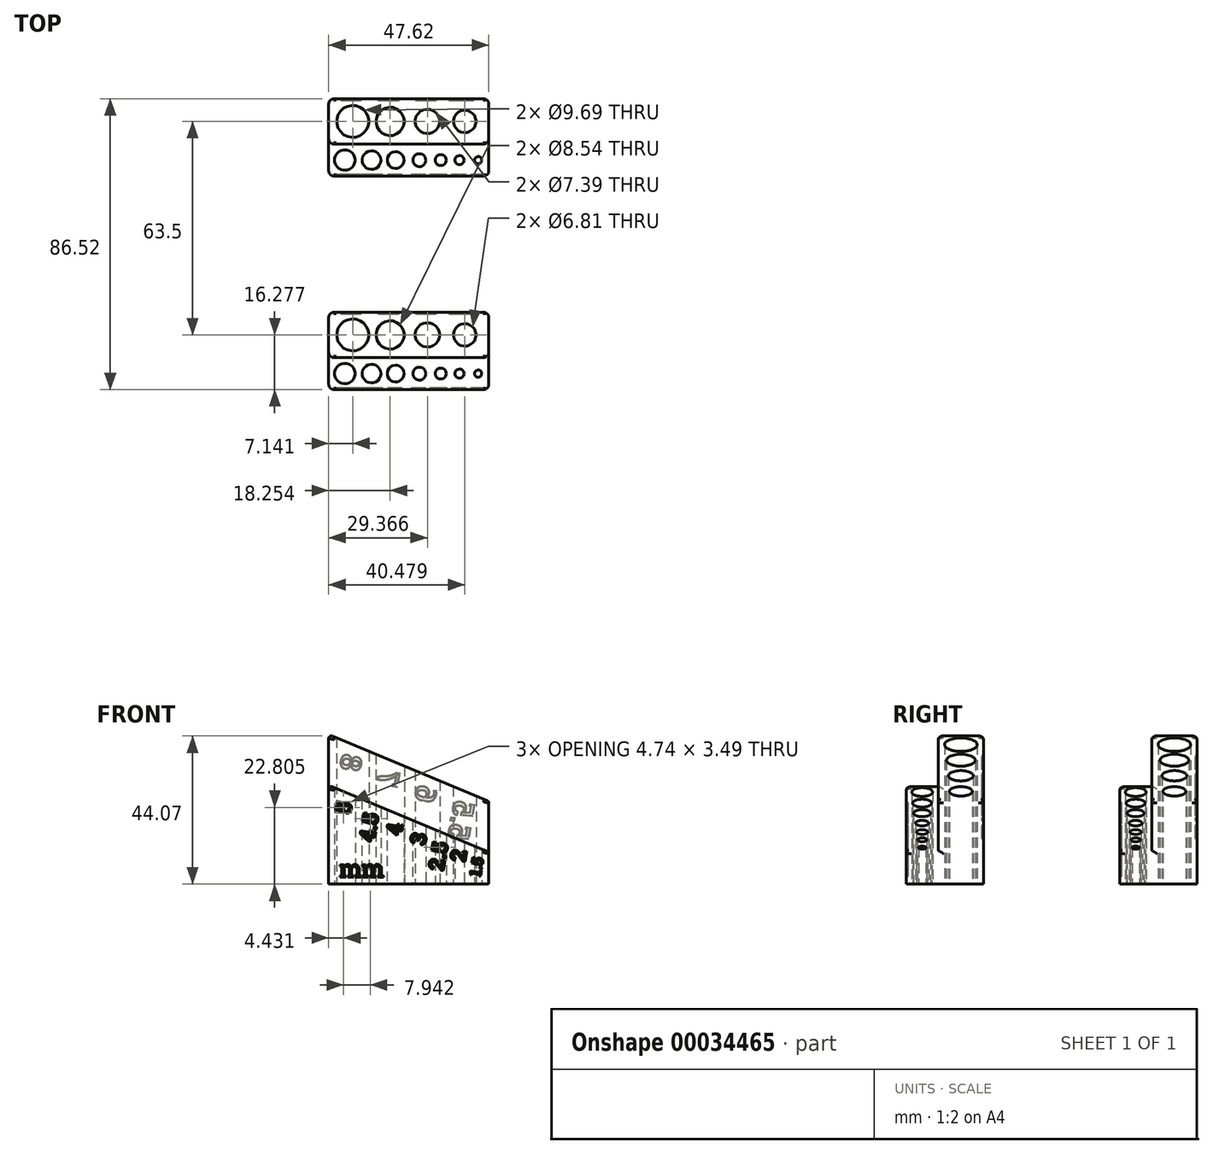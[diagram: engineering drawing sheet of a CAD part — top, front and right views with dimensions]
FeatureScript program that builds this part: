
annotation { "Feature Type Name" : "Feature", "Feature Type Description" : "" }
export const myFeature = defineFeature(function(context is Context, id is Id, definition is map)
    precondition{}
    {
        {
            var Q0;
            Q0=qCreatedBy(makeId("Front.planeOp"),FACE);
            var sketch = newSketch(context, id + "F0", { "sketchPlane" : qUnion([Q0])});
            skLineSegment(sketch, "E0", {"start": v(-23.81, 0) * mm, "end": v(23.81, 0) * mm});
            skLineSegment(sketch, "E1", {"start": v(23.81, 0) * mm, "end": v(23.81, 9.53) * mm});
            skLineSegment(sketch, "E2", {"start": v(23.81, 9.53) * mm, "end": v(-23.81, 29.37) * mm});
            skLineSegment(sketch, "E3", {"start": v(-23.81, 29.37) * mm, "end": v(-23.81, 0) * mm});
            skLineSegment(sketch, "E4", {"start": v(0, 0) * mm, "end": v(0, 19.45) * mm, "construction": true});
            skSolve(sketch);
        }
        {
            var Q0;
            Q0=qSketchRegion(id+"F0",true);
            extrude(context, id + "F1", {"entities" : qUnion([Q0]), "depth" : 9.52 * mm});
        }
        {
            var Q0;
            Q0=qCreatedBy(makeId("Front.planeOp"),FACE);
            var sketch = newSketch(context, id + "F2", { "sketchPlane" : qUnion([Q0])});
            skLineSegment(sketch, "E5.0", {"start": v(-23.81, 0) * mm, "end": v(23.81, 0) * mm});
            skLineSegment(sketch, "E6", {"start": v(23.81, 0) * mm, "end": v(23.81, 24.6) * mm});
            skLineSegment(sketch, "E7", {"start": v(-23.81, 0) * mm, "end": v(-23.81, 44.45) * mm});
            skLineSegment(sketch, "E8", {"start": v(-23.81, 44.45) * mm, "end": v(23.81, 24.6) * mm});
            skLineSegment(sketch, "E9.0", {"start": v(23.81, 9.52) * mm, "end": v(-23.81, 29.37) * mm, "construction": true});
            skSolve(sketch);
        }
        {
            var Q0;
            Q0=qSketchRegion(id+"F2",true);
            extrude(context, id + "F3", {"entities" : qUnion([Q0]), "operationType" : NewBodyOperationType.ADD, "oppositeDirection" : true, "depth" : 13.5 * mm});
        }
        {
            var Q0;
            Q0=qCreatedBy(makeId("Top.planeOp"),FACE);
            var sketch = newSketch(context, id + "F4", { "sketchPlane" : qUnion([Q0])});
            skLineSegment(sketch, "E10.0", {"start": v(23.81, 0) * mm, "end": v(-23.81, 0) * mm, "construction": true});
            skLineSegment(sketch, "E11.bottom", {"start": v(23.81, -9.53) * mm, "end": v(-23.81, -9.53) * mm, "construction": true});
            skLineSegment(sketch, "E11.top", {"start": v(23.81, 13.5) * mm, "end": v(-23.81, 13.5) * mm, "construction": true});
            skLineSegment(sketch, "E12", {"start": v(23.81, -4.76) * mm, "end": v(-23.81, -4.76) * mm, "construction": true});
            skLineSegment(sketch, "E13", {"start": v(23.81, -9.53) * mm, "end": v(23.81, 0) * mm, "construction": true});
            skLineSegment(sketch, "E14", {"start": v(-23.81, -9.53) * mm, "end": v(-23.81, 0) * mm, "construction": true});
            skLineSegment(sketch, "E15", {"start": v(-23.81, 13.5) * mm, "end": v(-23.81, 0) * mm, "construction": true});
            skLineSegment(sketch, "E16", {"start": v(23.81, 0) * mm, "end": v(23.81, 13.5) * mm, "construction": true});
            skCircle(sketch, "E17", {"center": v(20.64, -4.76) * mm, "radius": 0.87 * mm, "construction": true});
            skLineSegment(sketch, "E18", {"start": v(21.39, -5.2) * mm, "end": v(21.39, -4.33) * mm, "construction": true});
            skLineSegment(sketch, "E19", {"start": v(21.39, -4.33) * mm, "end": v(20.64, -3.9) * mm, "construction": true});
            skLineSegment(sketch, "E20", {"start": v(19.89, -5.2) * mm, "end": v(20.64, -5.63) * mm, "construction": true});
            skLineSegment(sketch, "E21", {"start": v(20.64, -5.63) * mm, "end": v(21.39, -5.2) * mm, "construction": true});
            skLineSegment(sketch, "E22", {"start": v(19.89, -5.2) * mm, "end": v(19.89, -4.33) * mm, "construction": true});
            skLineSegment(sketch, "E23", {"start": v(19.89, -4.33) * mm, "end": v(20.64, -3.9) * mm, "construction": true});
            skCircle(sketch, "E24", {"center": v(20.64, -4.76) * mm, "radius": 1.1 * mm});
            skLineSegment(sketch, "E25", {"start": v(20.64, -5.63) * mm, "end": v(20.64, -5.86) * mm, "construction": true});
            skCircle(sketch, "E26", {"center": v(15.08, -4.76) * mm, "radius": 1.15 * mm, "construction": true});
            skLineSegment(sketch, "E27", {"start": v(16.08, -5.34) * mm, "end": v(16.08, -4.19) * mm, "construction": true});
            skLineSegment(sketch, "E28", {"start": v(16.08, -4.19) * mm, "end": v(15.08, -3.6) * mm, "construction": true});
            skLineSegment(sketch, "E29", {"start": v(14.08, -5.34) * mm, "end": v(15.08, -5.92) * mm, "construction": true});
            skLineSegment(sketch, "E30", {"start": v(15.08, -5.92) * mm, "end": v(16.08, -5.34) * mm, "construction": true});
            skLineSegment(sketch, "E31", {"start": v(14.08, -5.34) * mm, "end": v(14.08, -4.19) * mm, "construction": true});
            skLineSegment(sketch, "E32", {"start": v(14.08, -4.19) * mm, "end": v(15.08, -3.6) * mm, "construction": true});
            skCircle(sketch, "E33", {"center": v(15.08, -4.76) * mm, "radius": 1.38 * mm});
            skLineSegment(sketch, "E34", {"start": v(15.08, -5.92) * mm, "end": v(15.08, -6.15) * mm, "construction": true});
            skCircle(sketch, "E35", {"center": v(9.52, -4.76) * mm, "radius": 1.44 * mm, "construction": true});
            skLineSegment(sketch, "E36", {"start": v(10.77, -5.48) * mm, "end": v(10.77, -4.04) * mm, "construction": true});
            skLineSegment(sketch, "E37", {"start": v(10.78, -4.04) * mm, "end": v(9.53, -3.32) * mm, "construction": true});
            skLineSegment(sketch, "E38", {"start": v(8.28, -5.48) * mm, "end": v(9.53, -6.2) * mm, "construction": true});
            skLineSegment(sketch, "E39", {"start": v(9.53, -6.2) * mm, "end": v(10.77, -5.48) * mm, "construction": true});
            skLineSegment(sketch, "E40", {"start": v(8.27, -5.48) * mm, "end": v(8.27, -4.04) * mm, "construction": true});
            skLineSegment(sketch, "E41", {"start": v(8.27, -4.04) * mm, "end": v(9.53, -3.32) * mm, "construction": true});
            skCircle(sketch, "E42", {"center": v(9.52, -4.76) * mm, "radius": 1.67 * mm});
            skLineSegment(sketch, "E43", {"start": v(9.53, -6.2) * mm, "end": v(9.53, -6.43) * mm, "construction": true});
            skCircle(sketch, "E44", {"center": v(3.17, -4.76) * mm, "radius": 1.73 * mm, "construction": true});
            skLineSegment(sketch, "E45", {"start": v(4.68, -5.63) * mm, "end": v(4.68, -3.9) * mm, "construction": true});
            skLineSegment(sketch, "E46", {"start": v(4.67, -3.9) * mm, "end": v(3.18, -3.03) * mm, "construction": true});
            skLineSegment(sketch, "E47", {"start": v(1.68, -5.63) * mm, "end": v(3.18, -6.5) * mm, "construction": true});
            skLineSegment(sketch, "E48", {"start": v(3.18, -6.5) * mm, "end": v(4.68, -5.63) * mm, "construction": true});
            skLineSegment(sketch, "E49", {"start": v(1.68, -5.63) * mm, "end": v(1.68, -3.9) * mm, "construction": true});
            skLineSegment(sketch, "E50", {"start": v(1.68, -3.9) * mm, "end": v(3.18, -3.03) * mm, "construction": true});
            skCircle(sketch, "E51", {"center": v(3.17, -4.76) * mm, "radius": 1.96 * mm});
            skLineSegment(sketch, "E52", {"start": v(3.18, -6.5) * mm, "end": v(3.18, -6.72) * mm, "construction": true});
            skCircle(sketch, "E53", {"center": v(-3.94, -4.76) * mm, "radius": 2.3 * mm, "construction": true});
            skLineSegment(sketch, "E54", {"start": v(-1.94, -5.92) * mm, "end": v(-1.94, -3.6) * mm, "construction": true});
            skLineSegment(sketch, "E55", {"start": v(-1.94, -3.6) * mm, "end": v(-3.94, -2.45) * mm, "construction": true});
            skLineSegment(sketch, "E56", {"start": v(-5.94, -5.92) * mm, "end": v(-3.94, -7.07) * mm, "construction": true});
            skLineSegment(sketch, "E57", {"start": v(-3.94, -7.07) * mm, "end": v(-1.94, -5.92) * mm, "construction": true});
            skLineSegment(sketch, "E58", {"start": v(-5.94, -5.92) * mm, "end": v(-5.94, -3.6) * mm, "construction": true});
            skLineSegment(sketch, "E59", {"start": v(-5.94, -3.6) * mm, "end": v(-3.94, -2.45) * mm, "construction": true});
            skCircle(sketch, "E60", {"center": v(-3.94, -4.76) * mm, "radius": 2.54 * mm});
            skLineSegment(sketch, "E61", {"start": v(-3.94, -7.07) * mm, "end": v(-3.94, -7.3) * mm, "construction": true});
            skCircle(sketch, "E62", {"center": v(-11.08, -4.76) * mm, "radius": 2.6 * mm, "construction": true});
            skLineSegment(sketch, "E63", {"start": v(-8.83, -6.06) * mm, "end": v(-8.83, -3.46) * mm, "construction": true});
            skLineSegment(sketch, "E64", {"start": v(-8.83, -3.46) * mm, "end": v(-11.08, -2.16) * mm, "construction": true});
            skLineSegment(sketch, "E65", {"start": v(-13.33, -6.06) * mm, "end": v(-11.08, -7.36) * mm, "construction": true});
            skLineSegment(sketch, "E66", {"start": v(-11.08, -7.36) * mm, "end": v(-8.83, -6.06) * mm, "construction": true});
            skLineSegment(sketch, "E67", {"start": v(-13.33, -6.06) * mm, "end": v(-13.33, -3.46) * mm, "construction": true});
            skLineSegment(sketch, "E68", {"start": v(-13.33, -3.46) * mm, "end": v(-11.08, -2.16) * mm, "construction": true});
            skCircle(sketch, "E69", {"center": v(-11.08, -4.76) * mm, "radius": 2.83 * mm});
            skLineSegment(sketch, "E70", {"start": v(-11.08, -7.36) * mm, "end": v(-11.08, -7.59) * mm, "construction": true});
            skCircle(sketch, "E71", {"center": v(16.67, 6.75) * mm, "radius": 3.18 * mm, "construction": true});
            skLineSegment(sketch, "E72", {"start": v(19.42, 5.16) * mm, "end": v(19.42, 8.33) * mm, "construction": true});
            skLineSegment(sketch, "E73", {"start": v(19.42, 8.33) * mm, "end": v(16.67, 9.92) * mm, "construction": true});
            skLineSegment(sketch, "E74", {"start": v(13.92, 5.16) * mm, "end": v(16.67, 3.57) * mm, "construction": true});
            skLineSegment(sketch, "E75", {"start": v(19.42, 5.16) * mm, "end": v(16.67, 3.57) * mm, "construction": true});
            skLineSegment(sketch, "E76", {"start": v(13.92, 5.16) * mm, "end": v(13.92, 8.33) * mm, "construction": true});
            skLineSegment(sketch, "E77", {"start": v(16.67, 9.92) * mm, "end": v(13.92, 8.33) * mm, "construction": true});
            skCircle(sketch, "E78", {"center": v(16.67, 6.75) * mm, "radius": 3.4 * mm});
            skLineSegment(sketch, "E79", {"start": v(16.67, 3.57) * mm, "end": v(16.67, 3.34) * mm, "construction": true});
            skCircle(sketch, "E80", {"center": v(5.56, 6.75) * mm, "radius": 3.46 * mm, "construction": true});
            skLineSegment(sketch, "E81", {"start": v(8.56, 5.01) * mm, "end": v(8.56, 8.48) * mm, "construction": true});
            skLineSegment(sketch, "E82", {"start": v(8.56, 8.48) * mm, "end": v(5.56, 10.21) * mm, "construction": true});
            skLineSegment(sketch, "E83", {"start": v(2.56, 5.01) * mm, "end": v(5.56, 3.28) * mm, "construction": true});
            skLineSegment(sketch, "E84", {"start": v(8.56, 5.01) * mm, "end": v(5.56, 3.28) * mm, "construction": true});
            skLineSegment(sketch, "E85", {"start": v(2.56, 5.01) * mm, "end": v(2.56, 8.48) * mm, "construction": true});
            skLineSegment(sketch, "E86", {"start": v(5.56, 10.21) * mm, "end": v(2.56, 8.48) * mm, "construction": true});
            skCircle(sketch, "E87", {"center": v(5.56, 6.75) * mm, "radius": 3.7 * mm});
            skLineSegment(sketch, "E88", {"start": v(5.56, 3.28) * mm, "end": v(5.56, 3.05) * mm, "construction": true});
            skCircle(sketch, "E89", {"center": v(-5.56, 6.75) * mm, "radius": 4.04 * mm, "construction": true});
            skLineSegment(sketch, "E90", {"start": v(-2.06, 4.73) * mm, "end": v(-2.06, 8.77) * mm, "construction": true});
            skLineSegment(sketch, "E91", {"start": v(-2.06, 8.77) * mm, "end": v(-5.56, 10.79) * mm, "construction": true});
            skLineSegment(sketch, "E92", {"start": v(-9.06, 4.73) * mm, "end": v(-5.56, 2.7) * mm, "construction": true});
            skLineSegment(sketch, "E93", {"start": v(-2.06, 4.73) * mm, "end": v(-5.56, 2.7) * mm, "construction": true});
            skLineSegment(sketch, "E94", {"start": v(-9.06, 4.73) * mm, "end": v(-9.06, 8.77) * mm, "construction": true});
            skLineSegment(sketch, "E95", {"start": v(-5.56, 10.79) * mm, "end": v(-9.06, 8.77) * mm, "construction": true});
            skCircle(sketch, "E96", {"center": v(-5.56, 6.75) * mm, "radius": 4.27 * mm});
            skLineSegment(sketch, "E97", {"start": v(-5.56, 2.7) * mm, "end": v(-5.56, 2.48) * mm, "construction": true});
            skCircle(sketch, "E98", {"center": v(-16.67, 6.75) * mm, "radius": 4.62 * mm, "construction": true});
            skLineSegment(sketch, "E99", {"start": v(-12.67, 4.44) * mm, "end": v(-12.67, 9.06) * mm, "construction": true});
            skLineSegment(sketch, "E100", {"start": v(-12.67, 9.06) * mm, "end": v(-16.67, 11.37) * mm, "construction": true});
            skLineSegment(sketch, "E101", {"start": v(-20.67, 4.44) * mm, "end": v(-16.67, 2.13) * mm, "construction": true});
            skLineSegment(sketch, "E102", {"start": v(-12.67, 4.44) * mm, "end": v(-16.67, 2.13) * mm, "construction": true});
            skLineSegment(sketch, "E103", {"start": v(-20.67, 4.44) * mm, "end": v(-20.67, 9.06) * mm, "construction": true});
            skLineSegment(sketch, "E104", {"start": v(-16.67, 11.37) * mm, "end": v(-20.67, 9.06) * mm, "construction": true});
            skCircle(sketch, "E105", {"center": v(-16.67, 6.75) * mm, "radius": 4.85 * mm});
            skLineSegment(sketch, "E106", {"start": v(-16.67, 2.13) * mm, "end": v(-16.67, 1.9) * mm, "construction": true});
            skLineSegment(sketch, "E107", {"start": v(-23.81, 6.75) * mm, "end": v(-16.67, 6.75) * mm, "construction": true});
            skLineSegment(sketch, "E108", {"start": v(-5.56, 6.75) * mm, "end": v(5.56, 6.75) * mm, "construction": true});
            skLineSegment(sketch, "E109", {"start": v(16.67, 6.75) * mm, "end": v(23.81, 6.75) * mm, "construction": true});
            skLineSegment(sketch, "E110", {"start": v(5.56, 6.75) * mm, "end": v(16.67, 6.75) * mm, "construction": true});
            skLineSegment(sketch, "E111", {"start": v(-5.56, 6.75) * mm, "end": v(-16.67, 6.75) * mm, "construction": true});
            skCircle(sketch, "E112", {"center": v(-19.02, -4.76) * mm, "radius": 2.89 * mm, "construction": true});
            skLineSegment(sketch, "E113", {"start": v(-16.52, -6.2) * mm, "end": v(-16.52, -3.32) * mm, "construction": true});
            skLineSegment(sketch, "E114", {"start": v(-16.52, -3.32) * mm, "end": v(-19.02, -1.88) * mm, "construction": true});
            skLineSegment(sketch, "E115", {"start": v(-21.52, -6.2) * mm, "end": v(-19.02, -7.65) * mm, "construction": true});
            skLineSegment(sketch, "E116", {"start": v(-19.02, -7.65) * mm, "end": v(-16.52, -6.2) * mm, "construction": true});
            skLineSegment(sketch, "E117", {"start": v(-21.52, -6.2) * mm, "end": v(-21.52, -3.32) * mm, "construction": true});
            skLineSegment(sketch, "E118", {"start": v(-21.52, -3.32) * mm, "end": v(-19.02, -1.88) * mm, "construction": true});
            skCircle(sketch, "E119", {"center": v(-19.02, -4.76) * mm, "radius": 3.12 * mm});
            skLineSegment(sketch, "E120", {"start": v(-19.02, -7.65) * mm, "end": v(-19.02, -7.88) * mm, "construction": true});
            skSolve(sketch);
        }
        {
            var Q0;
            Q0=qSketchRegion(id+"F4",true);
            extrude(context, id + "F5", {"entities" : qUnion([Q0]), "operationType" : NewBodyOperationType.REMOVE, "endBound" : BoundingType.THROUGH_ALL, "depth" : 25.4 * mm});
        }
        {
            var Q0;
            Q0=makeQuery(id+"F1.opExtrude","CAP_EDGE",EDGE,{"disambiguationData":[OSD([sQuery(id+"F0.wireOp",EDGE,"E1")])],"isStart":false});
            var Q1;
            Q1=makeQuery(id+"F3.opExtrude","CAP_EDGE",EDGE,{"disambiguationData":[OSD([sQuery(id+"F2.wireOp",EDGE,"E6")])],"isStart":true});
            var Q2;
            Q2=makeQuery(id+"F3.opExtrude","CAP_EDGE",EDGE,{"disambiguationData":[OSD([sQuery(id+"F2.wireOp",EDGE,"E6")])],"isStart":false});
            var Q3;
            Q3=makeQuery(id+"F3.opExtrude","CAP_EDGE",EDGE,{"disambiguationData":[OSD([sQuery(id+"F2.wireOp",EDGE,"E7")])],"isStart":true});
            var Q4;
            Q4=makeQuery(id+"F3.opExtrude","CAP_EDGE",EDGE,{"disambiguationData":[OSD([sQuery(id+"F2.wireOp",EDGE,"E7")])],"isStart":false});
            var Q5;
            Q5=makeQuery(id+"F1.opExtrude","CAP_EDGE",EDGE,{"disambiguationData":[OSD([sQuery(id+"F0.wireOp",EDGE,"E3")])],"isStart":false});
            fillet(context, id + "F6", {"entities" : qUnion([Q0, Q1, Q2, Q3, Q4, Q5]), "radius" : 1.59 * mm, "tangentPropagation" : true, "allowEdgeOverflow" : false});
        }
        {
            var Q0;
            Q0=makeQuery(id+"F3.opExtrude","CAP_EDGE",EDGE,{"disambiguationData":[OSD([sQuery(id+"F2.wireOp",EDGE,"E8")])],"isStart":true});
            var Q1;
            Q1=makeQuery(id+"F1.opExtrude","CAP_EDGE",EDGE,{"disambiguationData":[OSD([sQuery(id+"F0.wireOp",EDGE,"E2")])],"isStart":false});
            var Q2;
            Q2=makeQuery(id+"F1.opExtrude","CAP_EDGE",EDGE,{"disambiguationData":[OSD([sQuery(id+"F0.wireOp",EDGE,"E2")])],"isStart":true});
            fillet(context, id + "F7", {"entities" : qUnion([Q0, Q1, Q2]), "radius" : 0.76 * mm, "tangentPropagation" : true, "allowEdgeOverflow" : false});
        }
        {
            var Q0;
            Q0=makeQuery(id+"F1.opExtrude","CAP_FACE",FACE,{"disambiguationData":[OSD([sQuery(id+"F0.wireOp",EDGE,"E0"),sQuery(id+"F0.wireOp",EDGE,"E1"),sQuery(id+"F0.wireOp",EDGE,"E2"),sQuery(id+"F0.wireOp",EDGE,"E3")])],"isStart":false});
            var sketch = newSketch(context, id + "F8", { "sketchPlane" : qUnion([Q0])});
            skText(sketch, "E121", { "text": "1.5", "fontName": "RobotoSlab-Bold.ttf"});
            skText(sketch, "E122", { "text": "2", "fontName": "RobotoSlab-Bold.ttf"});
            skText(sketch, "E123", { "text": "2.5", "fontName": "RobotoSlab-Bold.ttf"});
            skText(sketch, "E124", { "text": "3", "fontName": "RobotoSlab-Bold.ttf"});
            skPoint(sketch, "E125", {"position": v(15.08, 10.41) * mm});
            skText(sketch, "E126", { "text": "4", "fontName": "RobotoSlab-Bold.ttf"});
            skText(sketch, "E127", { "text": "4.5", "fontName": "RobotoSlab-Bold.ttf"});
            skText(sketch, "E128", { "text": "5", "fontName": "RobotoSlab-Bold.ttf"});
            skPoint(sketch, "E129", {"position": v(20.64, 8.1) * mm});
            skPoint(sketch, "E130", {"position": v(9.53, 12.73) * mm});
            skPoint(sketch, "E131", {"position": v(3.17, 15.37) * mm});
            skPoint(sketch, "E132", {"position": v(-3.94, 18.34) * mm});
            skPoint(sketch, "E133", {"position": v(-11.08, 21.31) * mm});
            skPoint(sketch, "E134", {"position": v(-19.02, 24.62) * mm});
            skLineSegment(sketch, "E135", {"start": v(-19.02, 27.37) * mm, "end": v(-19.02, 24.62) * mm, "construction": true});
            skLineSegment(sketch, "E136.0", {"start": v(-22.13, 28.67) * mm, "end": v(-15.9, 26.07) * mm, "construction": true});
            skLineSegment(sketch, "E136.1", {"start": v(-13.9, 25.24) * mm, "end": v(-8.25, 22.89) * mm, "construction": true});
            skLineSegment(sketch, "E136.2", {"start": v(-6.48, 22.14) * mm, "end": v(-1.4, 20.03) * mm, "construction": true});
            skLineSegment(sketch, "E136.3", {"start": v(1.21, 18.94) * mm, "end": v(5.14, 17.3) * mm, "construction": true});
            skLineSegment(sketch, "E136.4", {"start": v(7.85, 16.17) * mm, "end": v(11.2, 14.78) * mm, "construction": true});
            skLineSegment(sketch, "E136.5", {"start": v(13.7, 13.74) * mm, "end": v(16.46, 12.59) * mm, "construction": true});
            skLineSegment(sketch, "E136.6", {"start": v(19.54, 11.3) * mm, "end": v(21.73, 10.4) * mm, "construction": true});
            skLineSegment(sketch, "E137", {"start": v(-11.08, 24.06) * mm, "end": v(-11.08, 21.31) * mm, "construction": true});
            skLineSegment(sketch, "E138", {"start": v(-3.94, 21.09) * mm, "end": v(-3.94, 18.34) * mm, "construction": true});
            skLineSegment(sketch, "E139", {"start": v(-23.81, 26.62) * mm, "end": v(23.81, 6.77) * mm, "construction": true});
            skLineSegment(sketch, "E140", {"start": v(3.17, 18.12) * mm, "end": v(3.17, 15.37) * mm, "construction": true});
            skLineSegment(sketch, "E141", {"start": v(9.52, 15.48) * mm, "end": v(9.52, 12.73) * mm, "construction": true});
            skLineSegment(sketch, "E142", {"start": v(20.64, 10.85) * mm, "end": v(20.64, 8.1) * mm, "construction": true});
            skLineSegment(sketch, "E143", {"start": v(15.08, 13.16) * mm, "end": v(15.08, 10.41) * mm, "construction": true});
            skText(sketch, "E144", { "text": "mm", "fontName": "RobotoSlab-Regular.ttf"});
            const initialGuessF8  = {"E121": [0.02126, 0.0021, 0.17365, 0.9848, 0.0033], "E122": [0.0167, 0.00637, 0.17365, 0.9848, 0.00457], "E123": [0.01026, 0.00372, 0.17365, 0.9848, 0.00457], "E124": [0.00479, 0.01134, 0.17365, 0.9848, 0.00457], "E126": [-0.00235, 0.0142, 0.17365, 0.9848, 0.00457], "E127": [-0.01036, 0.01224, 0.17365, 0.9848, 0.00457], "E128": [-0.0174, 0.02067, 0.17365, 0.9848, 0.00457], "E144": [-0.02064, 0.00203, 1, 0, 0.00508]};
            skSetInitialGuess(sketch, initialGuessF8);
            skSolve(sketch);
        }
        {
            var Q0;
            Q0 = qSketchRegion(id + "F8", true);
            extrude(context, id + "F9", {"entities" : qUnion([Q0]), "operationType" : NewBodyOperationType.REMOVE, "oppositeDirection" : true, "depth" : 0.5 * mm, "offsetDistance" : 25.4 * mm, "hasDraft" : true, "draftAngle" : 25 * degree, "draftPullDirection" : true});
        }
        {
            var Q0;
            Q0=makeQuery(id+"F3.opExtrude","CAP_FACE",FACE,{"disambiguationData":[OSD([sQuery(id+"F2.wireOp",EDGE,"E5.0"),sQuery(id+"F2.wireOp",EDGE,"E6"),sQuery(id+"F2.wireOp",EDGE,"E7"),sQuery(id+"F2.wireOp",EDGE,"E8")])],"isStart":false});
            var sketch = newSketch(context, id + "F10", { "sketchPlane" : qUnion([Q0])});
            skText(sketch, "E145", { "text": "5.5", "fontName": "RobotoSlab-Bold.ttf"});
            skPoint(sketch, "E146", {"position": v(-16.67, 24.83) * mm});
            skText(sketch, "E147", { "text": "6", "fontName": "RobotoSlab-Bold.ttf"});
            skPoint(sketch, "E148", {"position": v(-5.56, 29.46) * mm});
            skText(sketch, "E149", { "text": "7", "fontName": "RobotoSlab-Bold.ttf"});
            skPoint(sketch, "E150", {"position": v(5.56, 34.1) * mm});
            skText(sketch, "E151", { "text": "8", "fontName": "RobotoSlab-Bold.ttf"});
            skPoint(sketch, "E152", {"position": v(16.67, 38.72) * mm});
            skLineSegment(sketch, "E153", {"start": v(23.81, 41.7) * mm, "end": v(-23.81, 21.85) * mm, "construction": true});
            skLineSegment(sketch, "E154.0", {"start": v(21.52, 43.5) * mm, "end": v(11.82, 39.45) * mm, "construction": true});
            skLineSegment(sketch, "E154.1", {"start": v(9.83, 38.62) * mm, "end": v(1.29, 35.06) * mm, "construction": true});
            skLineSegment(sketch, "E154.2", {"start": v(-1.86, 33.75) * mm, "end": v(-9.25, 30.67) * mm, "construction": true});
            skLineSegment(sketch, "E154.3", {"start": v(-13.26, 29) * mm, "end": v(-20.07, 26.16) * mm, "construction": true});
            skLineSegment(sketch, "E155", {"start": v(-16.67, 27.58) * mm, "end": v(-16.67, 24.83) * mm, "construction": true});
            skLineSegment(sketch, "E156", {"start": v(-5.56, 32.21) * mm, "end": v(-5.56, 29.46) * mm, "construction": true});
            skLineSegment(sketch, "E157", {"start": v(5.56, 36.84) * mm, "end": v(5.56, 34.1) * mm, "construction": true});
            skLineSegment(sketch, "E158", {"start": v(16.67, 41.47) * mm, "end": v(16.67, 38.72) * mm, "construction": true});
            const initialGuessF10  = {"E145": [-0.01146, 0.0136, -0.17365, 0.9848, 0.00635], "E147": [-0.00151, 0.0248, -0.17365, 0.9848, 0.00635], "E149": [0.00958, 0.02954, -0.17365, 0.9848, 0.00635], "E151": [0.02068, 0.03425, -0.17365, 0.9848, 0.00635]};
            skSetInitialGuess(sketch, initialGuessF10);
            skSolve(sketch);
        }
        {
            var Q0;
            Q0 = qSketchRegion(id + "F10", true);
            extrude(context, id + "F11", {"entities" : qUnion([Q0]), "operationType" : NewBodyOperationType.REMOVE, "oppositeDirection" : true, "depth" : 0.5 * mm, "offsetDistance" : 25.4 * mm, "hasDraft" : true, "draftAngle" : 25 * degree, "draftPullDirection" : true});
        }
        {
            var Q0;
            Q0=makeQuery(id+"F1.opExtrude","SWEPT_BODY",BODY,{"disambiguationData":[OSD([sQuery(id+"F0.wireOp",EDGE,"E0"),sQuery(id+"F0.wireOp",EDGE,"E1"),sQuery(id+"F0.wireOp",EDGE,"E2"),sQuery(id+"F0.wireOp",EDGE,"E3")])]});
            var Q1;
            {var subQ0=sQuery(id+"F2.wireOp",EDGE,"E6");Q1=makeQuery(id+"F7.opFillet","BLEND_EDGE",EDGE,{"blendedFrom":[makeQuery(id+"F3.opExtrude","SWEPT_EDGE",EDGE,{"disambiguationData":[OSD([subQ0,sQuery(id+"F2.wireOp",EDGE,"E8")])]}),makeQuery(id+"F3.boolean.opBoolean","MERGE",FACE,{"derivedFrom":[makeQuery(id+"F1.opExtrude","SWEPT_FACE",FACE,{"disambiguationData":[OSD([sQuery(id+"F0.wireOp",EDGE,"E1")])]}),makeQuery(id+"F3.opExtrude","SWEPT_FACE",FACE,{"disambiguationData":[OSD([subQ0])]})]})],"blendedInto":[makeQuery(id+"F3.boolean.opBoolean","MERGE",FACE,{"derivedFrom":[makeQuery(id+"F1.opExtrude","SWEPT_FACE",FACE,{"disambiguationData":[OSD([sQuery(id+"F0.wireOp",EDGE,"E1")])]}),makeQuery(id+"F3.opExtrude","SWEPT_FACE",FACE,{"disambiguationData":[OSD([subQ0])]})]})]});}
            transform(context, id + "F12", {"entities" : qUnion([Q0]), "transformType" : TransformType.TRANSLATION_DISTANCE, "transformDirection" : qUnion([Q1]), "distance" : 63.5 * mm, "makeCopy" : true});
        }
    });
